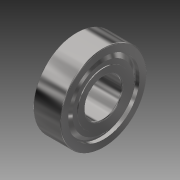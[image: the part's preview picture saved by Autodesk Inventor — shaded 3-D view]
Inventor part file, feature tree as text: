
AUTODESK INVENTOR PART (.ipt)
format: ipt  version: 2014 (Build 180170000, 170)  size: 392,704 bytes
history: native  units: in
note: dims shown in document units (in); Inventor stores cm internally (conversion verified against a paired STEP export)
features: other x4, imported_body x3, extrude x1, fillet x1, sketch x1
ambient origin geometry x8: Origin, YZ Plane, XZ Plane, XY Plane, X Axis, Y Axis, Z Axis, Center Point
bodies: Body1 (feature_tree), Body2 (feature_tree), Body3 (feature_tree)
feature tree (10):
  other  "R6ZZ"
  other  "R6ZZ1"
  extrude  "Extrusion1"  Depth=0.01in
  fillet  "Fillet1"  [1 undecoded]
  other  "R6ZZ_1"
  other  "R6ZZ_2"
  imported_body  "Base1"
  imported_body  "Base2"
  imported_body  "Base3"
  sketch  "Sketch1"  dims[d0=1.0in d1=0.0in d2=0.01in]
note: 1 required parameter value undecoded (feature->parameter linkage not recoverable at this tier; creation-order binding heuristic only, values carry confidence <= 0.55)
